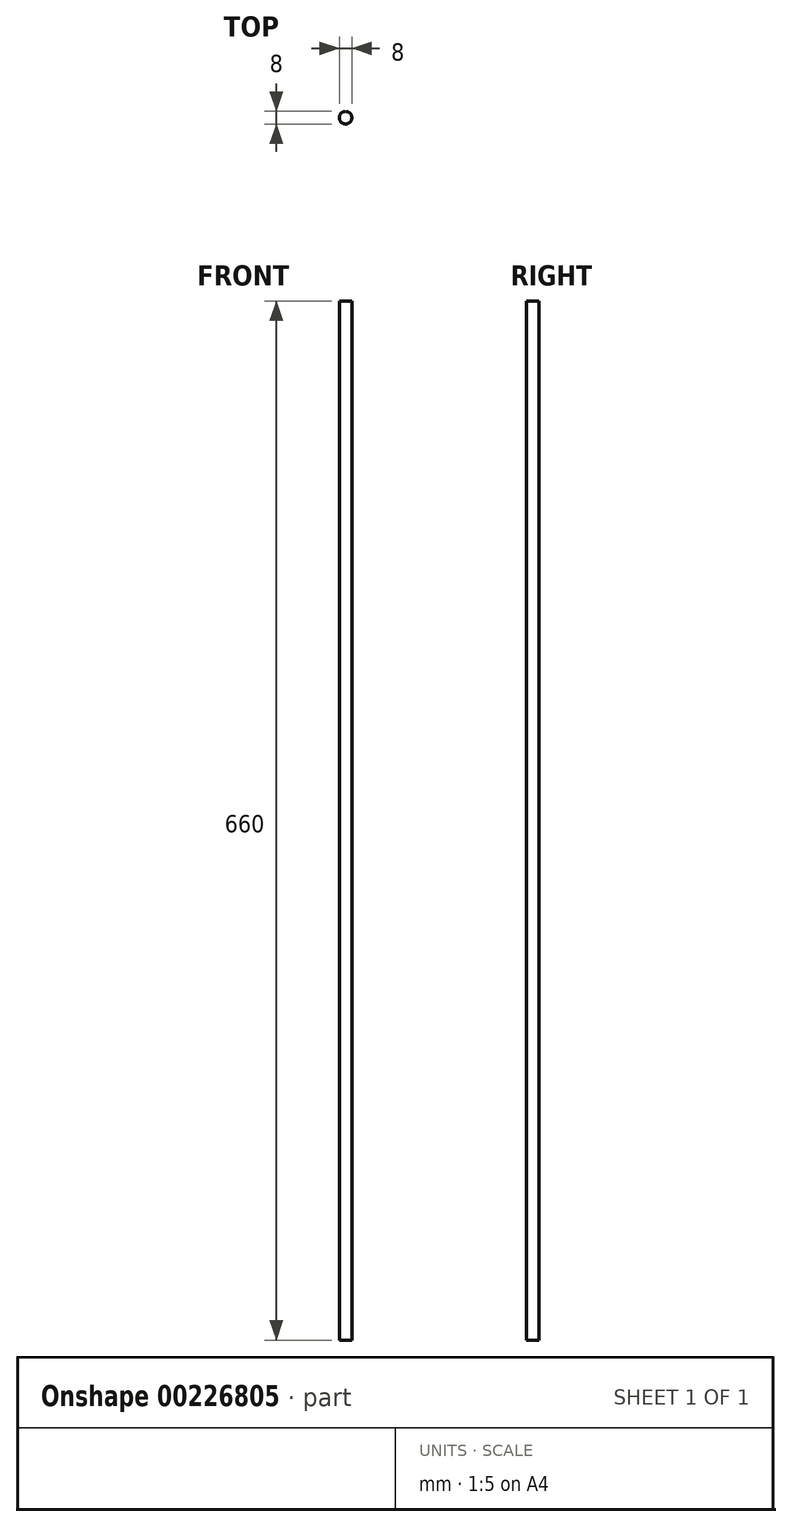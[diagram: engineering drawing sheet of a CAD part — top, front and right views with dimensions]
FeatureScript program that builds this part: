
annotation { "Feature Type Name" : "Feature", "Feature Type Description" : "" }
export const myFeature = defineFeature(function(context is Context, id is Id, definition is map)
    precondition{}
    {
        {
            var Q0;
            Q0=qCreatedBy(makeId("Top.planeOp"),FACE);
            var sketch = newSketch(context, id + "F0", { "sketchPlane" : qUnion([Q0])});
            skCircle(sketch, "E0", {"center": v(0, 0) * mm, "radius": 4 * mm});
            skSolve(sketch);
        }
        {
            var Q0;
            Q0 = qSketchRegion(id + "F0", true);
            extrude(context, id + "F1", {"entities" : qUnion([Q0]), "depth" : 660 * mm});
        }
    });
